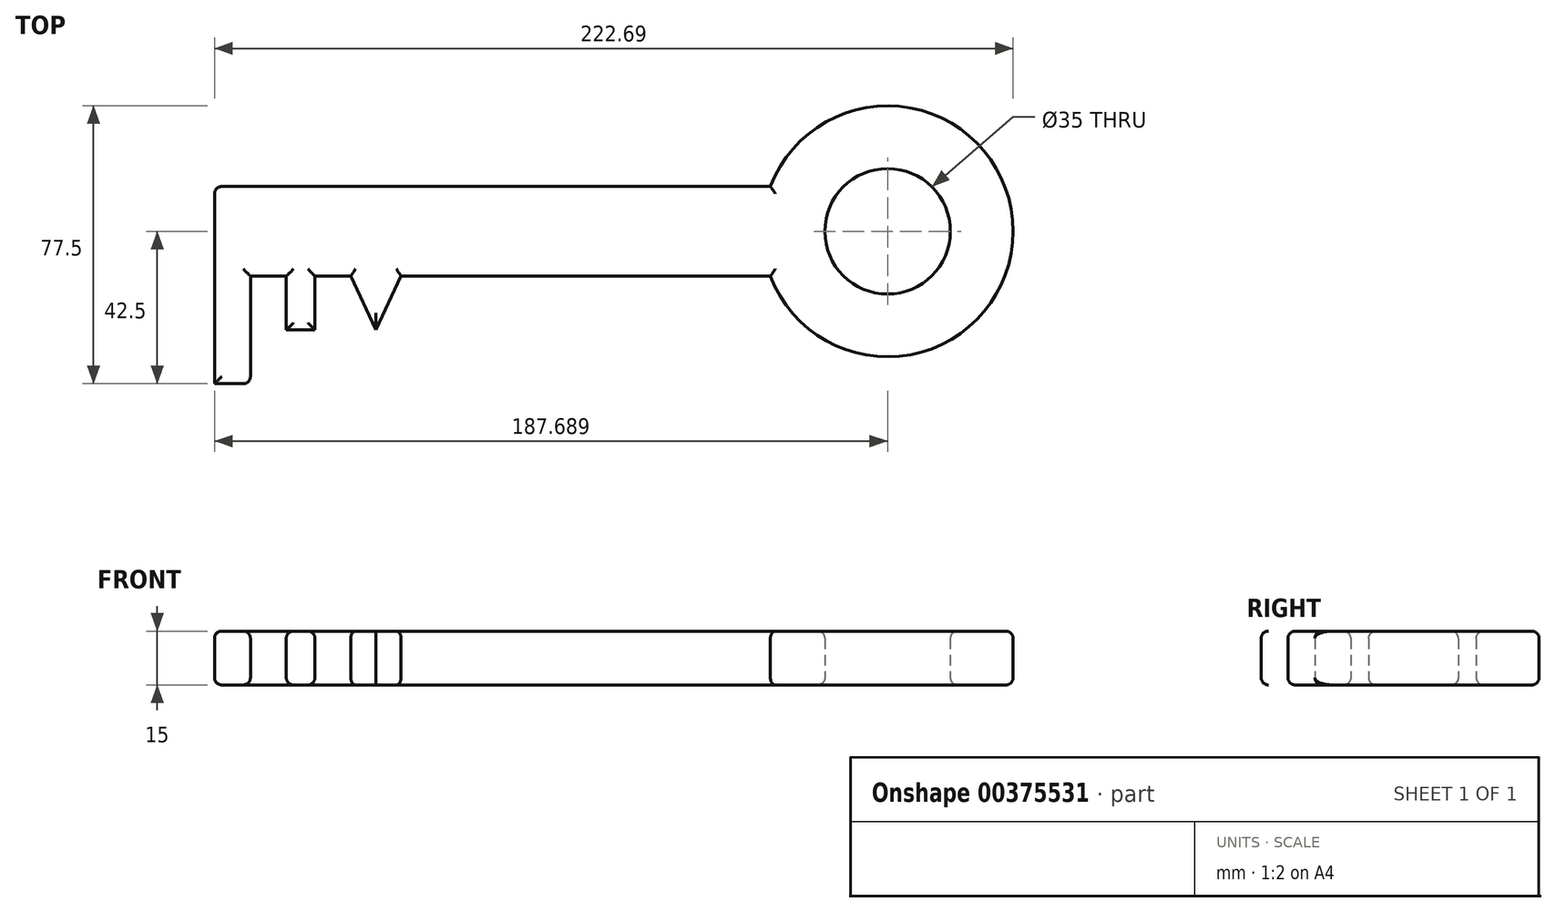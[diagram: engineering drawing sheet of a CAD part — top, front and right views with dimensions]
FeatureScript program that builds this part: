
annotation { "Feature Type Name" : "Feature", "Feature Type Description" : "" }
export const myFeature = defineFeature(function(context is Context, id is Id, definition is map)
    precondition{}
    {
        {
            var Q0;
            Q0=qCreatedBy(makeId("Top.planeOp"),FACE);
            var sketch = newSketch(context, id + "F0", { "sketchPlane" : qUnion([Q0])});
            skLineSegment(sketch, "E0.bottom", {"start": v(-129.44, 0) * mm, "end": v(25.56, 0) * mm});
            skLineSegment(sketch, "E0.top", {"start": v(-129.44, 25) * mm, "end": v(25.56, 25) * mm});
            skLineSegment(sketch, "E0.left", {"start": v(-129.44, 0) * mm, "end": v(-129.44, 25) * mm});
            skLineSegment(sketch, "E0.right", {"start": v(25.56, 0) * mm, "end": v(25.56, 25) * mm});
            skLineSegment(sketch, "E1.bottom", {"start": v(-129.44, 0) * mm, "end": v(-119.44, 0) * mm});
            skLineSegment(sketch, "E1.top", {"start": v(-129.44, -30) * mm, "end": v(-119.44, -30) * mm});
            skLineSegment(sketch, "E1.left", {"start": v(-129.44, 0) * mm, "end": v(-129.44, -30) * mm});
            skLineSegment(sketch, "E1.right", {"start": v(-119.44, 0) * mm, "end": v(-119.44, -30) * mm});
            skLineSegment(sketch, "E2.bottom", {"start": v(-109.44, 0) * mm, "end": v(-101.44, 0) * mm});
            skLineSegment(sketch, "E2.top", {"start": v(-109.44, -15) * mm, "end": v(-101.44, -15) * mm});
            skLineSegment(sketch, "E2.left", {"start": v(-109.44, 0) * mm, "end": v(-109.44, -15) * mm});
            skLineSegment(sketch, "E2.right", {"start": v(-101.44, 0) * mm, "end": v(-101.44, -15) * mm});
            skLineSegment(sketch, "E3", {"start": v(-91.44, 0) * mm, "end": v(-84.44, -15) * mm});
            skLineSegment(sketch, "E4", {"start": v(-84.44, -15) * mm, "end": v(-77.44, 0) * mm});
            skArc(sketch, "E5", {"start": v(25.56, 0) * mm, "mid": v(93.25, 12.5) * mm, "end": v(25.56, 25) * mm});
            skCircle(sketch, "E6", {"center": v(58.25, 12.5) * mm, "radius": 17.5 * mm});
            skLineSegment(sketch, "E7", {"start": v(58.25, 12.5) * mm, "end": v(-129.44, 12.5) * mm, "construction": true});
            skSolve(sketch);
        }
        {
            var Q0;
            Q0 = qSketchRegion(id + "F0", true);
            extrude(context, id + "F1", {"entities" : qUnion([Q0]), "depth" : 15 * mm});
        }
        {
            var Q0;
            {var subQ0=sQuery(id+"F0.wireOp",EDGE,"E0.bottom");Q0=makeQuery(id+"F1.opExtrude","CAP_EDGE",EDGE,{"disambiguationData":[OSD([subQ0]),TDD([makeQuery(id+"F0.imprint","IMPRINT",EDGE,{"disambiguationData":[TD([[makeQuery(id+"F0.imprint","INTERSECT",VERTEX,{"derivedFrom":[subQ0,sQuery(id+"F0.wireOp",EDGE,"E4")]}),-1.0]])],"derivedFrom":subQ0})])],"isStart":false});}
            var Q1;
            Q1=makeQuery(id+"F1.opExtrude","CAP_EDGE",EDGE,{"disambiguationData":[OSD([sQuery(id+"F0.wireOp",EDGE,"E4")])],"isStart":false});
            var Q2;
            Q2=makeQuery(id+"F1.opExtrude","CAP_EDGE",EDGE,{"disambiguationData":[OSD([sQuery(id+"F0.wireOp",EDGE,"E5")])],"isStart":false});
            var Q3;
            Q3=makeQuery(id+"F1.opExtrude","CAP_EDGE",EDGE,{"disambiguationData":[OSD([sQuery(id+"F0.wireOp",EDGE,"E0.top")])],"isStart":false});
            var Q4;
            Q4=makeQuery(id+"F1.opExtrude","CAP_EDGE",EDGE,{"disambiguationData":[OSD([sQuery(id+"F0.wireOp",EDGE,"E3")])],"isStart":false});
            var Q5;
            {var subQ0=sQuery(id+"F0.wireOp",EDGE,"E0.bottom");Q5=makeQuery(id+"F1.opExtrude","CAP_EDGE",EDGE,{"disambiguationData":[OSD([subQ0]),TDD([makeQuery(id+"F0.imprint","IMPRINT",EDGE,{"disambiguationData":[TD([[makeQuery(id+"F0.imprint","INTERSECT",VERTEX,{"derivedFrom":[subQ0,sQuery(id+"F0.wireOp",EDGE,"E3")]}),1.0]])],"derivedFrom":subQ0})])],"isStart":false});}
            var Q6;
            Q6=makeQuery(id+"F1.opExtrude","CAP_EDGE",EDGE,{"disambiguationData":[OSD([sQuery(id+"F0.wireOp",EDGE,"E2.right")])],"isStart":false});
            var Q7;
            {var subQ0=sQuery(id+"F0.wireOp",EDGE,"E0.bottom");Q7=makeQuery(id+"F1.opExtrude","CAP_EDGE",EDGE,{"disambiguationData":[OSD([subQ0]),TDD([makeQuery(id+"F0.imprint","IMPRINT",EDGE,{"disambiguationData":[TD([[makeQuery(id+"F0.imprint","INTERSECT",VERTEX,{"derivedFrom":[subQ0,sQuery(id+"F0.wireOp",EDGE,"E1.bottom"),sQuery(id+"F0.wireOp",EDGE,"E1.right")]}),-1.0]])],"derivedFrom":subQ0})])],"isStart":false});}
            var Q8;
            Q8=makeQuery(id+"F1.opExtrude","CAP_EDGE",EDGE,{"disambiguationData":[OSD([sQuery(id+"F0.wireOp",EDGE,"E1.right")])],"isStart":false});
            var Q9;
            Q9=makeQuery(id+"F1.opExtrude","CAP_EDGE",EDGE,{"disambiguationData":[OSD([sQuery(id+"F0.wireOp",EDGE,"E0.left"),sQuery(id+"F0.wireOp",EDGE,"E1.left")])],"isStart":false});
            var Q10;
            Q10=makeQuery(id+"F1.opExtrude","CAP_FACE",FACE,{"disambiguationData":[OSD([sQuery(id+"F0.wireOp",EDGE,"E0.bottom"),sQuery(id+"F0.wireOp",EDGE,"E0.top"),sQuery(id+"F0.wireOp",EDGE,"E0.left"),sQuery(id+"F0.wireOp",EDGE,"E1.top"),sQuery(id+"F0.wireOp",EDGE,"E1.left"),sQuery(id+"F0.wireOp",EDGE,"E1.right"),sQuery(id+"F0.wireOp",EDGE,"E2.top"),sQuery(id+"F0.wireOp",EDGE,"E2.left"),sQuery(id+"F0.wireOp",EDGE,"E2.right"),sQuery(id+"F0.wireOp",EDGE,"E3"),sQuery(id+"F0.wireOp",EDGE,"E4"),sQuery(id+"F0.wireOp",EDGE,"E5"),sQuery(id+"F0.wireOp",EDGE,"E6")])],"isStart":false});
            var Q11;
            Q11=makeQuery(id+"F1.opExtrude","CAP_EDGE",EDGE,{"disambiguationData":[OSD([sQuery(id+"F0.wireOp",EDGE,"E6")])],"isStart":false});
            var Q12;
            Q12=makeQuery(id+"F1.opExtrude","CAP_EDGE",EDGE,{"disambiguationData":[OSD([sQuery(id+"F0.wireOp",EDGE,"E1.top")])],"isStart":true});
            var Q13;
            Q13=makeQuery(id+"F1.opExtrude","CAP_EDGE",EDGE,{"disambiguationData":[OSD([sQuery(id+"F0.wireOp",EDGE,"E1.right")])],"isStart":true});
            var Q14;
            Q14=makeQuery(id+"F1.opExtrude","CAP_EDGE",EDGE,{"disambiguationData":[OSD([sQuery(id+"F0.wireOp",EDGE,"E0.left"),sQuery(id+"F0.wireOp",EDGE,"E1.left")])],"isStart":true});
            var Q15;
            Q15=makeQuery(id+"F1.opExtrude","CAP_EDGE",EDGE,{"disambiguationData":[OSD([sQuery(id+"F0.wireOp",EDGE,"E0.top")])],"isStart":true});
            var Q16;
            {var subQ0=sQuery(id+"F0.wireOp",EDGE,"E0.bottom");Q16=makeQuery(id+"F1.opExtrude","CAP_EDGE",EDGE,{"disambiguationData":[OSD([subQ0]),TDD([makeQuery(id+"F0.imprint","IMPRINT",EDGE,{"disambiguationData":[TD([[makeQuery(id+"F0.imprint","INTERSECT",VERTEX,{"derivedFrom":[subQ0,sQuery(id+"F0.wireOp",EDGE,"E1.bottom"),sQuery(id+"F0.wireOp",EDGE,"E1.right")]}),-1.0]])],"derivedFrom":subQ0})])],"isStart":true});}
            var Q17;
            Q17=makeQuery(id+"F1.opExtrude","CAP_EDGE",EDGE,{"disambiguationData":[OSD([sQuery(id+"F0.wireOp",EDGE,"E2.left")])],"isStart":true});
            var Q18;
            Q18=makeQuery(id+"F1.opExtrude","CAP_EDGE",EDGE,{"disambiguationData":[OSD([sQuery(id+"F0.wireOp",EDGE,"E2.top")])],"isStart":true});
            var Q19;
            Q19=makeQuery(id+"F1.opExtrude","CAP_EDGE",EDGE,{"disambiguationData":[OSD([sQuery(id+"F0.wireOp",EDGE,"E3")])],"isStart":true});
            var Q20;
            {var subQ0=sQuery(id+"F0.wireOp",EDGE,"E0.bottom");Q20=makeQuery(id+"F1.opExtrude","CAP_EDGE",EDGE,{"disambiguationData":[OSD([subQ0]),TDD([makeQuery(id+"F0.imprint","IMPRINT",EDGE,{"disambiguationData":[TD([[makeQuery(id+"F0.imprint","INTERSECT",VERTEX,{"derivedFrom":[subQ0,sQuery(id+"F0.wireOp",EDGE,"E3")]}),1.0]])],"derivedFrom":subQ0})])],"isStart":true});}
            var Q21;
            Q21=makeQuery(id+"F1.opExtrude","CAP_EDGE",EDGE,{"disambiguationData":[OSD([sQuery(id+"F0.wireOp",EDGE,"E2.right")])],"isStart":true});
            var Q22;
            {var subQ0=sQuery(id+"F0.wireOp",EDGE,"E0.bottom");Q22=makeQuery(id+"F1.opExtrude","CAP_EDGE",EDGE,{"disambiguationData":[OSD([subQ0]),TDD([makeQuery(id+"F0.imprint","IMPRINT",EDGE,{"disambiguationData":[TD([[makeQuery(id+"F0.imprint","INTERSECT",VERTEX,{"derivedFrom":[subQ0,sQuery(id+"F0.wireOp",EDGE,"E4")]}),-1.0]])],"derivedFrom":subQ0})])],"isStart":true});}
            var Q23;
            Q23=makeQuery(id+"F1.opExtrude","CAP_EDGE",EDGE,{"disambiguationData":[OSD([sQuery(id+"F0.wireOp",EDGE,"E4")])],"isStart":true});
            var Q24;
            Q24=makeQuery(id+"F1.opExtrude","CAP_EDGE",EDGE,{"disambiguationData":[OSD([sQuery(id+"F0.wireOp",EDGE,"E5")])],"isStart":true});
            var Q25;
            Q25=makeQuery(id+"F1.opExtrude","CAP_EDGE",EDGE,{"disambiguationData":[OSD([sQuery(id+"F0.wireOp",EDGE,"E6")])],"isStart":true});
            var Q26;
            Q26=makeQuery(id+"F1.opExtrude","SWEPT_EDGE",EDGE,{"disambiguationData":[OSD([sQuery(id+"F0.wireOp",EDGE,"E0.top"),sQuery(id+"F0.wireOp",EDGE,"E0.left")])]});
            var Q27;
            Q27=makeQuery(id+"F1.opExtrude","SWEPT_EDGE",EDGE,{"disambiguationData":[OSD([sQuery(id+"F0.wireOp",EDGE,"E1.top"),sQuery(id+"F0.wireOp",EDGE,"E1.right")])]});
            fillet(context, id + "F2", {"entities" : qUnion([Q0, Q1, Q2, Q3, Q4, Q5, Q6, Q7, Q8, Q9, Q10, Q11, Q12, Q13, Q14, Q15, Q16, Q17, Q18, Q19, Q20, Q21, Q22, Q23, Q24, Q25, Q26, Q27]), "radius" : 2 * mm, "tangentPropagation" : true, "allowEdgeOverflow" : false});
        }
    });
